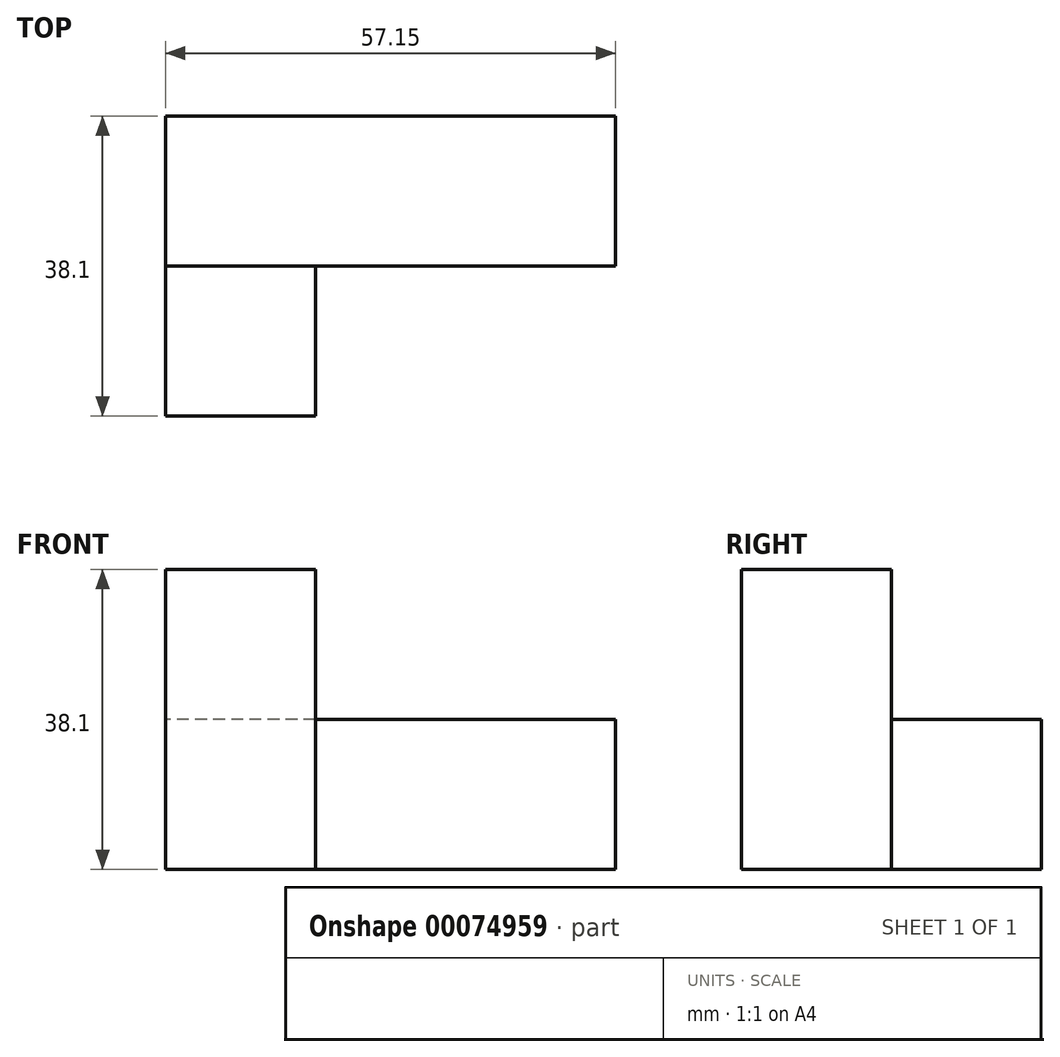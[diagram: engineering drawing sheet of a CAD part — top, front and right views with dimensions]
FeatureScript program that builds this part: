
annotation { "Feature Type Name" : "Feature", "Feature Type Description" : "" }
export const myFeature = defineFeature(function(context is Context, id is Id, definition is map)
    precondition{}
    {
        {
            var Q0;
            Q0=qCreatedBy(makeId("Front.planeOp"),FACE);
            var sketch = newSketch(context, id + "F0", { "sketchPlane" : qUnion([Q0])});
            skLineSegment(sketch, "E0.bottom", {"start": v(0, 0) * mm, "end": v(-57.15, 0) * mm});
            skLineSegment(sketch, "E0.top", {"start": v(0, 19.05) * mm, "end": v(-57.15, 19.05) * mm});
            skLineSegment(sketch, "E0.left", {"start": v(0, 0) * mm, "end": v(0, 19.05) * mm});
            skLineSegment(sketch, "E0.right", {"start": v(-57.15, 0) * mm, "end": v(-57.15, 19.05) * mm});
            skSolve(sketch);
        }
        {
            var Q0;
            Q0=qSketchRegion(id+"F0",true);
            extrude(context, id + "F1", {"entities" : qUnion([Q0]), "depth" : 19.05 * mm});
        }
        {
            var Q0;
            Q0=makeQuery(id+"F1.opExtrude","CAP_FACE",FACE,{"disambiguationData":[OSD([sQuery(id+"F0.wireOp",EDGE,"E0.bottom"),sQuery(id+"F0.wireOp",EDGE,"E0.top"),sQuery(id+"F0.wireOp",EDGE,"E0.left"),sQuery(id+"F0.wireOp",EDGE,"E0.right")])],"isStart":false});
            var sketch = newSketch(context, id + "F2", { "sketchPlane" : qUnion([Q0])});
            skLineSegment(sketch, "E1.bottom", {"start": v(-57.15, 19.05) * mm, "end": v(-38.1, 19.05) * mm});
            skLineSegment(sketch, "E1.top", {"start": v(-57.15, 0) * mm, "end": v(-38.1, 0) * mm});
            skLineSegment(sketch, "E1.left", {"start": v(-57.15, 19.05) * mm, "end": v(-57.15, 0) * mm});
            skLineSegment(sketch, "E1.right", {"start": v(-38.1, 19.05) * mm, "end": v(-38.1, 0) * mm});
            skSolve(sketch);
        }
        {
            var Q0;
            Q0=qSketchRegion(id+"F2",true);
            extrude(context, id + "F3", {"entities" : qUnion([Q0]), "operationType" : NewBodyOperationType.ADD, "depth" : 19.05 * mm});
        }
        {
            var Q0;
            Q0=makeQuery(id+"F3.boolean.opBoolean","MERGE",FACE,{"derivedFrom":[makeQuery(id+"F1.opExtrude","SWEPT_FACE",FACE,{"disambiguationData":[OSD([sQuery(id+"F0.wireOp",EDGE,"E0.top")])]}),makeQuery(id+"F3.opExtrude","SWEPT_FACE",FACE,{"disambiguationData":[OSD([sQuery(id+"F2.wireOp",EDGE,"E1.bottom")])]})]});
            var sketch = newSketch(context, id + "F4", { "sketchPlane" : qUnion([Q0])});
            skSolve(sketch);
        }
        {
            var Q0;
            {var subQ1=sQuery(id+"F0.wireOp",EDGE,"E0.top");Q0=makeQuery(id+"F4.imprint","IMPRINT",FACE,{"disambiguationData":[TD([[makeQuery(id+"F4.imprint","IMPRINT",EDGE,{"derivedFrom":makeQuery(id+"F1.opExtrude","CAP_EDGE",EDGE,{"disambiguationData":[OSD([subQ1])],"isStart":true})}),1.0]])]});}
            var sketch = newSketch(context, id + "F5", { "sketchPlane" : qUnion([Q0])});
            skLineSegment(sketch, "E2.bottom", {"start": v(-38.1, -38.1) * mm, "end": v(-57.15, -38.1) * mm});
            skLineSegment(sketch, "E2.top", {"start": v(-38.1, -19.05) * mm, "end": v(-57.15, -19.05) * mm});
            skLineSegment(sketch, "E2.left", {"start": v(-38.1, -38.1) * mm, "end": v(-38.1, -19.05) * mm});
            skLineSegment(sketch, "E2.right", {"start": v(-57.15, -38.1) * mm, "end": v(-57.15, -19.05) * mm});
            skSolve(sketch);
        }
        {
            var Q0;
            Q0=qSketchRegion(id+"F5",true);
            extrude(context, id + "F6", {"entities" : qUnion([Q0]), "operationType" : NewBodyOperationType.ADD, "depth" : 19.05 * mm});
        }
    });
